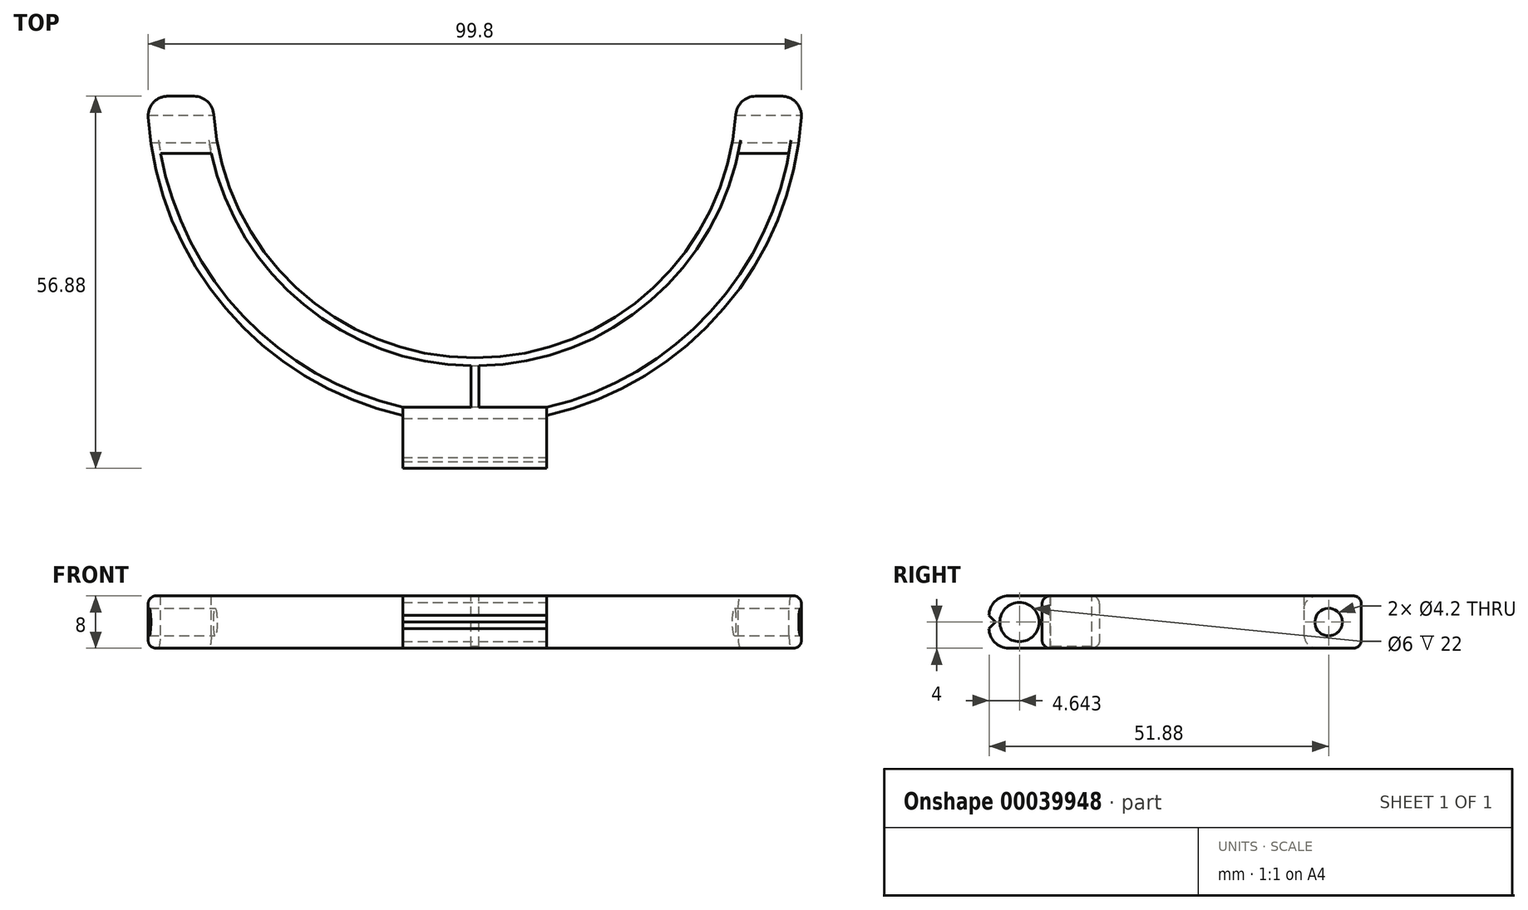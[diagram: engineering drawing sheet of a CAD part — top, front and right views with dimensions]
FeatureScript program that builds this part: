
annotation { "Feature Type Name" : "Feature", "Feature Type Description" : "" }
export const myFeature = defineFeature(function(context is Context, id is Id, definition is map)
    precondition{}
    {
        {
            var Q0;
            Q0=qCreatedBy(makeId("Top.planeOp"),FACE);
            var sketch = newSketch(context, id + "F0", { "sketchPlane" : qUnion([Q0])});
            skArc(sketch, "E0", {"start": v(-50, 0) * mm, "mid": v(0, -50) * mm, "end": v(50, 0) * mm});
            skArc(sketch, "E1", {"start": v(-40, 0) * mm, "mid": v(0, -40) * mm, "end": v(40, 0) * mm});
            skLineSegment(sketch, "E2", {"start": v(-50, 0) * mm, "end": v(50, 0) * mm});
            skLineSegment(sketch, "E3", {"start": v(-11, -48.77) * mm, "end": v(-11, -56.88) * mm});
            skLineSegment(sketch, "E4", {"start": v(-11, -56.88) * mm, "end": v(0, -56.88) * mm});
            skLineSegment(sketch, "E5", {"start": v(0, -56.88) * mm, "end": v(11, -56.88) * mm});
            skPoint(sketch, "E5.endSnap0", {"position": v(-5.5, -56.88) * mm});
            skLineSegment(sketch, "E6", {"start": v(11, -56.88) * mm, "end": v(11, -48.77) * mm});
            skSolve(sketch);
        }
        {
            var Q0;
            {var subQ1=sQuery(id+"F0.wireOp",EDGE,"E1");Q0=makeQuery(id+"F0.imprint","IMPRINT",FACE,{"disambiguationData":[TD([[makeQuery(id+"F0.imprint","IMPRINT",EDGE,{"derivedFrom":subQ1}),-1.0]])]});}
            var Q1;
            {var subQ1=sQuery(id+"F0.wireOp",EDGE,"E3");Q1=makeQuery(id+"F0.imprint","IMPRINT",FACE,{"disambiguationData":[TD([[makeQuery(id+"F0.imprint","IMPRINT",EDGE,{"derivedFrom":subQ1}),1.0]])]});}
            extrude(context, id + "F1", {"entities" : qUnion([Q0, Q1]), "depth" : 8 * mm});
        }
        {
            var Q0;
            Q0=qCreatedBy(makeId("Right.planeOp"),FACE);
            cPlane(context, id + "F2", {"entities" : qUnion([Q0]), "cplaneType" : CPlaneType.OFFSET, "offset" : 50 * mm, "width" : 150 * mm, "height" : 150 * mm});
        }
        {
            var Q0;
            Q0=qCreatedBy(id+"F2.planeOp",FACE);
            var sketch = newSketch(context, id + "F3", { "sketchPlane" : qUnion([Q0])});
            skCircle(sketch, "E7", {"center": v(-5, 4) * mm, "radius": 2.1 * mm});
            skSolve(sketch);
        }
        {
            var Q0;
            Q0 = qSketchRegion(id + "F3", true);
            extrude(context, id + "F4", {"entities" : qUnion([Q0]), "operationType" : NewBodyOperationType.REMOVE, "endBound" : BoundingType.THROUGH_ALL, "oppositeDirection" : true, "depth" : 25 * mm});
        }
        {
            var Q0;
            {var subQ0=sQuery(id+"F0.wireOp",EDGE,"E0");var subQ1=sQuery(id+"F0.wireOp",EDGE,"E2");Q0=makeQuery(id+"F1.opExtrude","SWEPT_EDGE",EDGE,{"disambiguationData":[OSD([subQ0,subQ1]),TDD([makeQuery(id+"F0.imprint","INTERSECT",VERTEX,{"disambiguationData":[OD(1.0)],"derivedFrom":[subQ0,subQ1]})])]});}
            var Q1;
            {var subQ0=sQuery(id+"F0.wireOp",EDGE,"E1");var subQ1=sQuery(id+"F0.wireOp",EDGE,"E2");Q1=makeQuery(id+"F1.opExtrude","SWEPT_EDGE",EDGE,{"disambiguationData":[OSD([subQ0,subQ1]),TDD([makeQuery(id+"F0.imprint","INTERSECT",VERTEX,{"disambiguationData":[OD(1.0)],"derivedFrom":[subQ0,subQ1]})])]});}
            var Q2;
            {var subQ0=sQuery(id+"F0.wireOp",EDGE,"E1");var subQ1=sQuery(id+"F0.wireOp",EDGE,"E2");Q2=makeQuery(id+"F1.opExtrude","SWEPT_EDGE",EDGE,{"disambiguationData":[OSD([subQ0,subQ1]),TDD([makeQuery(id+"F0.imprint","INTERSECT",VERTEX,{"disambiguationData":[OD(0.0)],"derivedFrom":[subQ0,subQ1]})])]});}
            var Q3;
            {var subQ0=sQuery(id+"F0.wireOp",EDGE,"E0");var subQ1=sQuery(id+"F0.wireOp",EDGE,"E2");Q3=makeQuery(id+"F1.opExtrude","SWEPT_EDGE",EDGE,{"disambiguationData":[OSD([subQ0,subQ1]),TDD([makeQuery(id+"F0.imprint","INTERSECT",VERTEX,{"disambiguationData":[OD(0.0)],"derivedFrom":[subQ0,subQ1]})])]});}
            var Q4;
            Q4=makeQuery(id+"F1.opExtrude","CAP_EDGE",EDGE,{"disambiguationData":[OSD([sQuery(id+"F0.wireOp",EDGE,"E4"),sQuery(id+"F0.wireOp",EDGE,"E5")])],"isStart":false});
            var Q5;
            Q5=makeQuery(id+"F1.opExtrude","CAP_EDGE",EDGE,{"disambiguationData":[OSD([sQuery(id+"F0.wireOp",EDGE,"E4"),sQuery(id+"F0.wireOp",EDGE,"E5")])],"isStart":true});
            fillet(context, id + "F5", {"entities" : qUnion([Q0, Q1, Q2, Q3, Q4, Q5]), "radius" : 3 * mm, "tangentPropagation" : true, "allowEdgeOverflow" : false});
        }
        {
            var Q0;
            {var subQ0=sQuery(id+"F0.wireOp",EDGE,"E0");Q0=makeQuery(id+"F1.opExtrude","CAP_EDGE",EDGE,{"disambiguationData":[OSD([subQ0]),TDD([makeQuery(id+"F0.imprint","IMPRINT",EDGE,{"disambiguationData":[TD([[makeQuery(id+"F0.imprint","INTERSECT",VERTEX,{"disambiguationData":[OD(1.0)],"derivedFrom":[subQ0,sQuery(id+"F0.wireOp",EDGE,"E2")]}),1.0]])],"derivedFrom":subQ0})])],"isStart":false});}
            var Q1;
            {var subQ0=sQuery(id+"F0.wireOp",EDGE,"E0");Q1=makeQuery(id+"F1.opExtrude","CAP_EDGE",EDGE,{"disambiguationData":[OSD([subQ0]),TDD([makeQuery(id+"F0.imprint","IMPRINT",EDGE,{"disambiguationData":[TD([[makeQuery(id+"F0.imprint","INTERSECT",VERTEX,{"disambiguationData":[OD(1.0)],"derivedFrom":[subQ0,sQuery(id+"F0.wireOp",EDGE,"E2")]}),1.0]])],"derivedFrom":subQ0})])],"isStart":true});}
            fillet(context, id + "F6", {"entities" : qUnion([Q0, Q1]), "radius" : 1.2 * mm, "tangentPropagation" : true, "allowEdgeOverflow" : false});
        }
        {
            var Q0;
            Q0=makeQuery(id+"F1.opExtrude","SWEPT_FACE",FACE,{"disambiguationData":[OSD([sQuery(id+"F0.wireOp",EDGE,"E6")])]});
            var sketch = newSketch(context, id + "F7", { "sketchPlane" : qUnion([Q0])});
            skCircle(sketch, "E8", {"center": v(-52.24, 4) * mm, "radius": 3 * mm});
            skSolve(sketch);
        }
        {
            var Q0;
            Q0 = qSketchRegion(id + "F7", true);
            extrude(context, id + "F8", {"entities" : qUnion([Q0]), "operationType" : NewBodyOperationType.REMOVE, "endBound" : BoundingType.THROUGH_ALL, "oppositeDirection" : true, "depth" : 25 * mm});
        }
        {
            var Q0;
            Q0=makeQuery(id+"F1.opExtrude","SWEPT_FACE",FACE,{"disambiguationData":[OSD([sQuery(id+"F0.wireOp",EDGE,"E4"),sQuery(id+"F0.wireOp",EDGE,"E5")])]});
            extrude(context, id + "F9", {"entities" : qUnion([Q0]), "operationType" : NewBodyOperationType.REMOVE, "oppositeDirection" : true, "depth" : 1.4 * mm});
        }
        {
            var Q0;
            {var subQ0=sQuery(id+"F0.wireOp",EDGE,"E5");var subQ1=sQuery(id+"F0.wireOp",EDGE,"E4");Q0=makeQuery(id+"F9.boolean.opBoolean","COPY",EDGE,{"derivedFrom":makeQuery(id+"F9.opExtrude","CAP_EDGE",EDGE,{"disambiguationData":[OSD([subQ1,subQ0]),TDD([makeQuery(id+"F5.opFillet","BLEND_EDGE",EDGE,{"blendedFrom":[makeQuery(id+"F1.opExtrude","CAP_EDGE",EDGE,{"disambiguationData":[OSD([subQ1,subQ0])],"isStart":true}),makeQuery(id+"F1.opExtrude","SWEPT_FACE",FACE,{"disambiguationData":[OSD([subQ1,subQ0])]})],"blendedInto":[makeQuery(id+"F1.opExtrude","SWEPT_FACE",FACE,{"disambiguationData":[OSD([subQ1,subQ0])]})]})])],"isStart":false})});}
            var Q1;
            {var subQ0=sQuery(id+"F0.wireOp",EDGE,"E5");var subQ1=sQuery(id+"F0.wireOp",EDGE,"E4");Q1=makeQuery(id+"F9.boolean.opBoolean","COPY",EDGE,{"derivedFrom":makeQuery(id+"F9.opExtrude","CAP_EDGE",EDGE,{"disambiguationData":[OSD([subQ1,subQ0]),TDD([makeQuery(id+"F5.opFillet","BLEND_EDGE",EDGE,{"blendedFrom":[makeQuery(id+"F1.opExtrude","CAP_EDGE",EDGE,{"disambiguationData":[OSD([subQ1,subQ0])],"isStart":false}),makeQuery(id+"F1.opExtrude","SWEPT_FACE",FACE,{"disambiguationData":[OSD([subQ1,subQ0])]})],"blendedInto":[makeQuery(id+"F1.opExtrude","SWEPT_FACE",FACE,{"disambiguationData":[OSD([subQ1,subQ0])]})]})])],"isStart":false})});}
            chamfer(context, id + "F10", {"entities" : qUnion([Q0, Q1]), "width" : 1.4 * mm, "tangentPropagation" : true});
        }
        {
            var Q0;
            Q0=makeQuery(id+"F1.opExtrude","CAP_FACE",FACE,{"disambiguationData":[OSD([sQuery(id+"F0.wireOp",EDGE,"E0"),sQuery(id+"F0.wireOp",EDGE,"E1"),sQuery(id+"F0.wireOp",EDGE,"E2"),sQuery(id+"F0.wireOp",EDGE,"E3"),sQuery(id+"F0.wireOp",EDGE,"E4"),sQuery(id+"F0.wireOp",EDGE,"E5"),sQuery(id+"F0.wireOp",EDGE,"E6")])],"isStart":false});
            var sketch = newSketch(context, id + "F11", { "sketchPlane" : qUnion([Q0])});
            skLineSegment(sketch, "E9", {"start": v(-11, -47.54) * mm, "end": v(11, -47.54) * mm});
            skLineSegment(sketch, "E10", {"start": v(-48.01, -8.73) * mm, "end": v(-40.26, -8.73) * mm});
            skLineSegment(sketch, "E11", {"start": v(40.26, -8.73) * mm, "end": v(48.01, -8.73) * mm});
            skSolve(sketch);
        }
        {
            var Q0;
            Q0=makeQuery(id+"F11.imprint","IMPRINT",FACE,{"disambiguationData":[TD([[makeQuery(id+"F11.imprint","IMPRINT",EDGE,{"derivedFrom":sQuery(id+"F11.wireOp",EDGE,"E9")}),1.0]])]});
            extrude(context, id + "F12", {"entities" : qUnion([Q0]), "operationType" : NewBodyOperationType.REMOVE, "endBound" : BoundingType.THROUGH_ALL, "oppositeDirection" : true, "depth" : 25 * mm});
        }
        {
            var Q0;
            Q0=makeQuery(id+"F12.boolean.opBoolean","COPY",EDGE,{"derivedFrom":makeQuery(id+"F12.opExtrude","CAP_EDGE",EDGE,{"disambiguationData":[OSD([sQuery(id+"F11.wireOp",EDGE,"E10")])],"isStart":true})});
            var Q1;
            Q1=makeQuery(id+"F12.boolean.opBoolean","INTERSECT",EDGE,{"derivedFrom":[makeQuery(id+"F1.opExtrude","CAP_FACE",FACE,{"disambiguationData":[OSD([sQuery(id+"F0.wireOp",EDGE,"E0"),sQuery(id+"F0.wireOp",EDGE,"E1"),sQuery(id+"F0.wireOp",EDGE,"E2"),sQuery(id+"F0.wireOp",EDGE,"E3"),sQuery(id+"F0.wireOp",EDGE,"E4"),sQuery(id+"F0.wireOp",EDGE,"E5"),sQuery(id+"F0.wireOp",EDGE,"E6")])],"isStart":true}),makeQuery(id+"F12.opExtrude","SWEPT_FACE",FACE,{"disambiguationData":[OSD([sQuery(id+"F11.wireOp",EDGE,"E10")])]})]});
            var Q2;
            Q2=makeQuery(id+"F12.boolean.opBoolean","COPY",EDGE,{"derivedFrom":makeQuery(id+"F12.opExtrude","CAP_EDGE",EDGE,{"disambiguationData":[OSD([sQuery(id+"F11.wireOp",EDGE,"E11")])],"isStart":true})});
            var Q3;
            Q3=makeQuery(id+"F12.boolean.opBoolean","INTERSECT",EDGE,{"derivedFrom":[makeQuery(id+"F1.opExtrude","CAP_FACE",FACE,{"disambiguationData":[OSD([sQuery(id+"F0.wireOp",EDGE,"E0"),sQuery(id+"F0.wireOp",EDGE,"E1"),sQuery(id+"F0.wireOp",EDGE,"E2"),sQuery(id+"F0.wireOp",EDGE,"E3"),sQuery(id+"F0.wireOp",EDGE,"E4"),sQuery(id+"F0.wireOp",EDGE,"E5"),sQuery(id+"F0.wireOp",EDGE,"E6")])],"isStart":true}),makeQuery(id+"F12.opExtrude","SWEPT_FACE",FACE,{"disambiguationData":[OSD([sQuery(id+"F11.wireOp",EDGE,"E11")])]})]});
            fillet(context, id + "F13", {"entities" : qUnion([Q0, Q1, Q2, Q3]), "radius" : 2 * mm, "tangentPropagation" : true, "allowEdgeOverflow" : false});
        }
        {
            var Q0;
            Q0=makeQuery(id+"F12.boolean.opBoolean","COPY",FACE,{"derivedFrom":makeQuery(id+"F12.opExtrude","SWEPT_FACE",FACE,{"disambiguationData":[OSD([sQuery(id+"F11.wireOp",EDGE,"E9")])]})});
            var sketch = newSketch(context, id + "F14", { "sketchPlane" : qUnion([Q0])});
            skLineSegment(sketch, "E12.rect.bottom", {"start": v(-0.6, 8) * mm, "end": v(0.6, 8) * mm});
            skLineSegment(sketch, "E12.rect.top", {"start": v(-0.6, 0.28) * mm, "end": v(0.6, 0.28) * mm});
            skLineSegment(sketch, "E12.rect.left", {"start": v(-0.6, 8) * mm, "end": v(-0.6, 0.28) * mm});
            skLineSegment(sketch, "E12.rect.right", {"start": v(0.6, 8) * mm, "end": v(0.6, 0.28) * mm});
            skPoint(sketch, "E12.rect.middle", {"position": v(0, 4.14) * mm});
            skSolve(sketch);
        }
        {
            var Q0;
            Q0 = qSketchRegion(id + "F14", true);
            var Q1;
            {var subQ0=sQuery(id+"F0.wireOp",EDGE,"E6");var subQ1=sQuery(id+"F0.wireOp",EDGE,"E5");var subQ2=sQuery(id+"F0.wireOp",EDGE,"E4");var subQ3=sQuery(id+"F0.wireOp",EDGE,"E3");var subQ4=sQuery(id+"F0.wireOp",EDGE,"E2");var subQ5=sQuery(id+"F0.wireOp",EDGE,"E1");var subQ6=sQuery(id+"F0.wireOp",EDGE,"E0");var subQ7=makeQuery(id+"F6.opFillet","BLEND_EDGE",EDGE,{"blendedFrom":[makeQuery(id+"F1.opExtrude","CAP_EDGE",EDGE,{"disambiguationData":[OSD([subQ5])],"isStart":false}),makeQuery(id+"F1.opExtrude","CAP_FACE",FACE,{"disambiguationData":[OSD([subQ6,subQ5,subQ4,subQ3,subQ2,subQ1,subQ0])],"isStart":false})],"blendedInto":[makeQuery(id+"F1.opExtrude","CAP_FACE",FACE,{"disambiguationData":[OSD([subQ6,subQ5,subQ4,subQ3,subQ2,subQ1,subQ0])],"isStart":false})]});Q1=makeQuery(id+"F12.boolean.opBoolean","COPY",FACE,{"derivedFrom":makeQuery(id+"F12.opExtrude","SWEPT_FACE",FACE,{"disambiguationData":[OSD([subQ6,subQ5,subQ4,subQ3,subQ2,subQ1,subQ0]),TDD([makeQuery(id+"F11.imprint","IMPRINT",EDGE,{"disambiguationData":[TD([[makeQuery(id+"F11.imprint","INTERSECT",VERTEX,{"derivedFrom":[subQ7,sQuery(id+"F11.wireOp",EDGE,"E10")]}),1.0]])],"derivedFrom":subQ7})])]})});}
            extrude(context, id + "F15", {"entities" : qUnion([Q0]), "operationType" : NewBodyOperationType.ADD, "endBound" : BoundingType.UP_TO_SURFACE, "endBoundEntityFace" : qUnion([Q1]), "depth" : 25 * mm});
        }
    });
